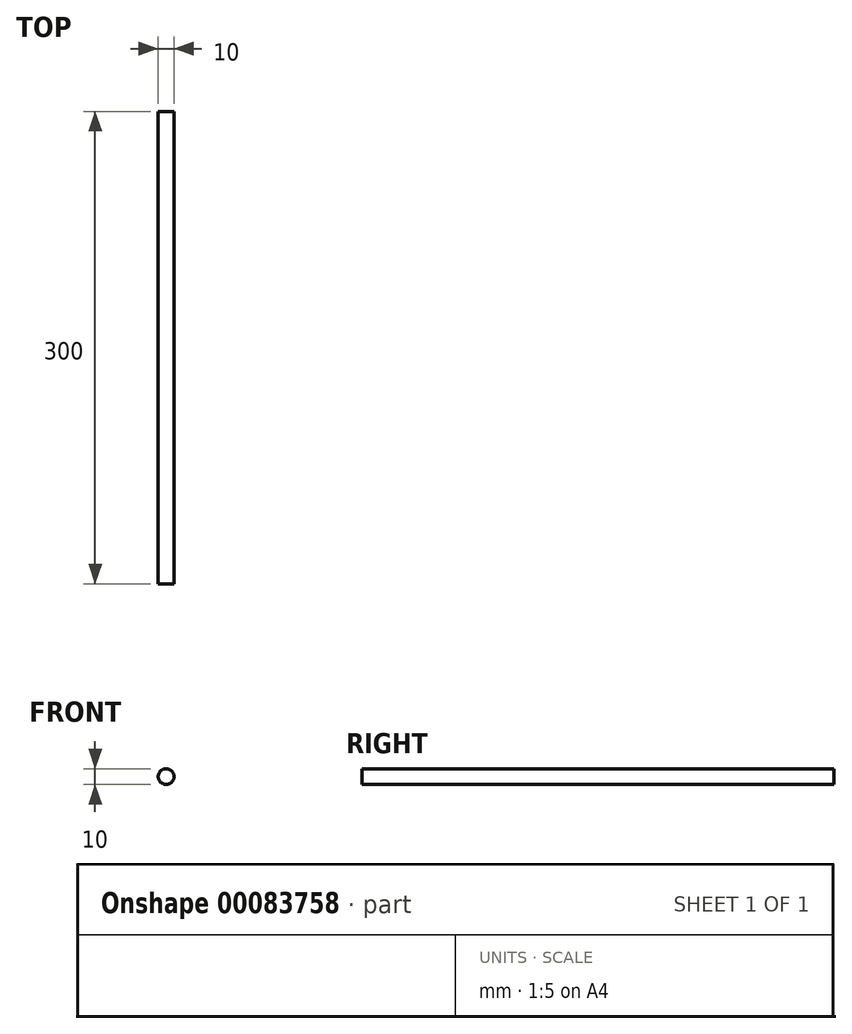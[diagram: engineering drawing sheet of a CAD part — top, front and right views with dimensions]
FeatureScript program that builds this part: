
annotation { "Feature Type Name" : "Feature", "Feature Type Description" : "" }
export const myFeature = defineFeature(function(context is Context, id is Id, definition is map)
    precondition{}
    {
        {
            var Q0;
            Q0=qCreatedBy(makeId("Front.planeOp"),FACE);
            var sketch = newSketch(context, id + "F0", { "sketchPlane" : qUnion([Q0])});
            skCircle(sketch, "E0", {"center": v(0, 0) * mm, "radius": 5 * mm});
            skSolve(sketch);
        }
        {
            var Q0;
            Q0 = qSketchRegion(id + "F0", true);
            extrude(context, id + "F1", {"entities" : qUnion([Q0]), "depth" : 150 * mm, "hasSecondDirection" : true, "secondDirectionOppositeDirection" : true, "secondDirectionDepth" : 150 * mm});
        }
    });
